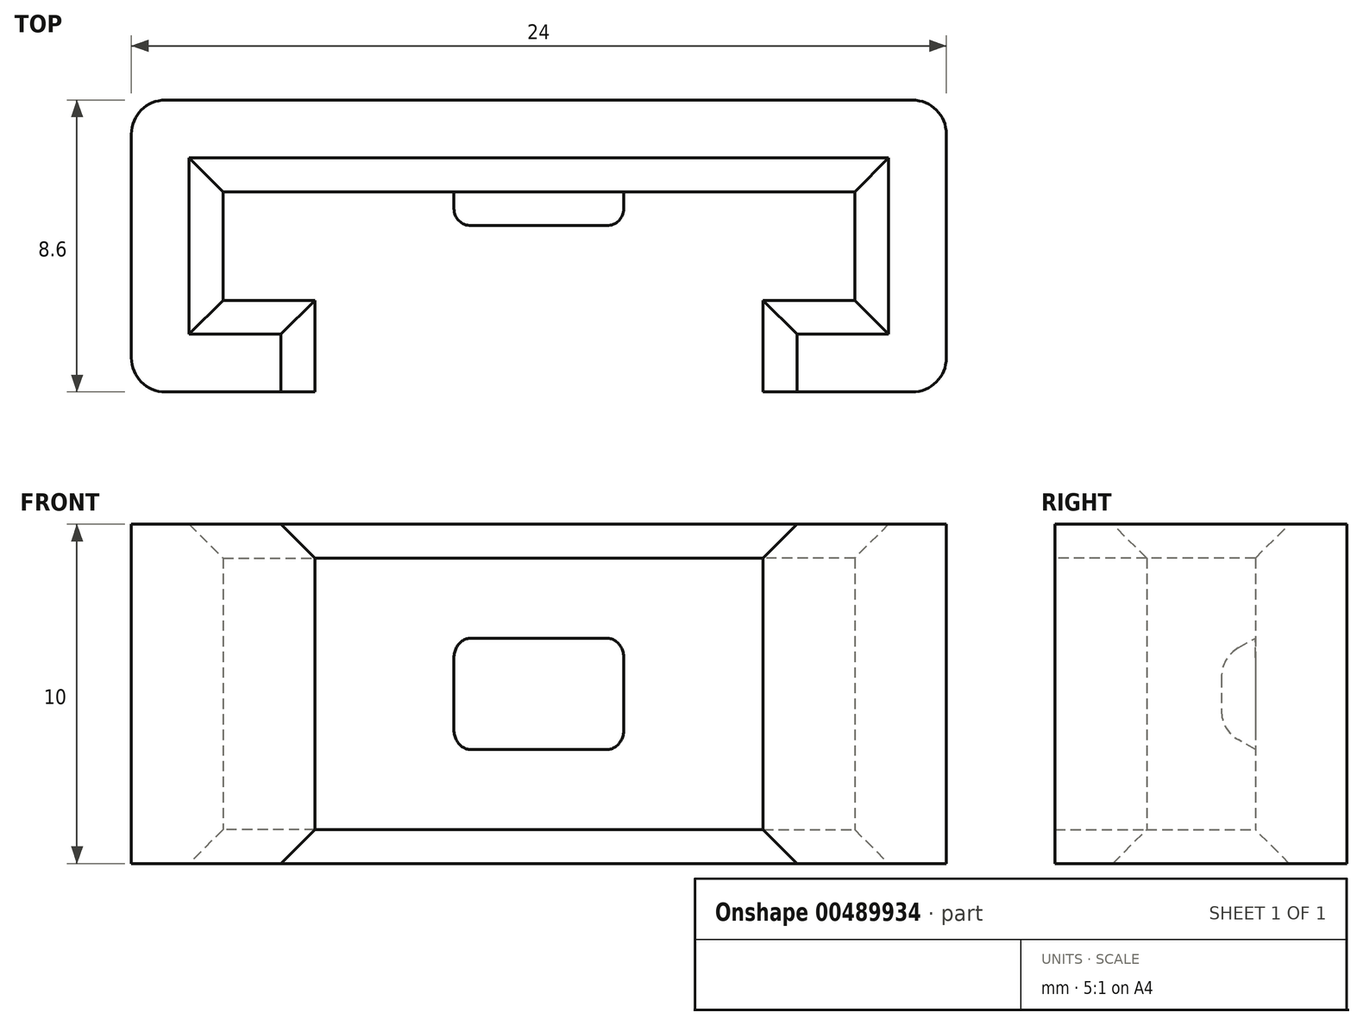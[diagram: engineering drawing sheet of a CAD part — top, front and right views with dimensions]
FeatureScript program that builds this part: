
annotation { "Feature Type Name" : "Feature", "Feature Type Description" : "" }
export const myFeature = defineFeature(function(context is Context, id is Id, definition is map)
    precondition{}
    {
        {
            var Q0;
            Q0=qCreatedBy(makeId("Top.planeOp"),FACE);
            var sketch = newSketch(context, id + "F0", { "sketchPlane" : qUnion([Q0])});
            skLineSegment(sketch, "E0", {"start": v(0, -17.47) * mm, "end": v(0, 25.01) * mm, "construction": true});
            skLineSegment(sketch, "E1", {"start": v(-9.3, -5.9) * mm, "end": v(-6.6, -5.9) * mm});
            skLineSegment(sketch, "E2", {"start": v(-6.6, -5.9) * mm, "end": v(-6.6, -8.6) * mm});
            skLineSegment(sketch, "E3", {"start": v(-6.6, -8.6) * mm, "end": v(-12, -8.6) * mm});
            skLineSegment(sketch, "E4", {"start": v(-12, -8.6) * mm, "end": v(-12, 0) * mm});
            skLineSegment(sketch, "E5", {"start": v(-12, 0) * mm, "end": v(0, 0) * mm});
            skLineSegment(sketch, "E6", {"start": v(-9.3, -5.9) * mm, "end": v(-9.3, -2.7) * mm});
            skLineSegment(sketch, "E7", {"start": v(-9.3, -2.7) * mm, "end": v(0, -2.7) * mm});
            skLineSegment(sketch, "E8.MirrorCS", {"start": v(9.3, -5.9) * mm, "end": v(6.6, -5.9) * mm});
            skLineSegment(sketch, "E9.MirrorCS", {"start": v(9.3, -5.9) * mm, "end": v(9.3, -2.7) * mm});
            skLineSegment(sketch, "E10.MirrorCS", {"start": v(6.6, -5.9) * mm, "end": v(6.6, -8.6) * mm});
            skLineSegment(sketch, "E11.MirrorCS", {"start": v(12, -8.6) * mm, "end": v(12, 0) * mm});
            skLineSegment(sketch, "E12.MirrorCS", {"start": v(6.6, -8.6) * mm, "end": v(12, -8.6) * mm});
            skLineSegment(sketch, "E13.MirrorCS", {"start": v(12, 0) * mm, "end": v(0, 0) * mm});
            skLineSegment(sketch, "E14.MirrorCS", {"start": v(9.3, -2.7) * mm, "end": v(0, -2.7) * mm});
            skSolve(sketch);
        }
        {
            var Q0;
            Q0=qSketchRegion(id+"F0",true);
            extrude(context, id + "F1", {"entities" : qUnion([Q0]), "depth" : 10 * mm});
        }
        {
            var Q0;
            Q0=makeQuery(id+"F1.opExtrude","SWEPT_FACE",FACE,{"disambiguationData":[OSD([sQuery(id+"F0.wireOp",EDGE,"E7"),sQuery(id+"F0.wireOp",EDGE,"E14.MirrorCS")])]});
            var sketch = newSketch(context, id + "F2", { "sketchPlane" : qUnion([Q0])});
            skLineSegment(sketch, "E15", {"start": v(0, 0) * mm, "end": v(0, 10) * mm, "construction": true});
            skLineSegment(sketch, "E16.bottom", {"start": v(2.5, 6.7) * mm, "end": v(-2.5, 6.7) * mm});
            skLineSegment(sketch, "E16.top", {"start": v(2.5, 3.3) * mm, "end": v(-2.5, 3.3) * mm});
            skLineSegment(sketch, "E16.left", {"start": v(2.5, 6.7) * mm, "end": v(2.5, 3.3) * mm});
            skLineSegment(sketch, "E16.right", {"start": v(-2.5, 6.7) * mm, "end": v(-2.5, 3.3) * mm});
            skPoint(sketch, "E16.middle", {"position": v(0, 5) * mm});
            skSolve(sketch);
        }
        {
            var Q0;
            Q0=qSketchRegion(id+"F2",true);
            extrude(context, id + "F3", {"entities" : qUnion([Q0]), "operationType" : NewBodyOperationType.ADD, "depth" : 1 * mm});
        }
        {
            var Q0;
            Q0=makeQuery(id+"F3.opExtrude","CAP_EDGE",EDGE,{"disambiguationData":[OSD([sQuery(id+"F2.wireOp",EDGE,"E16.bottom")])],"isStart":false});
            var Q1;
            Q1=makeQuery(id+"F3.opExtrude","CAP_EDGE",EDGE,{"disambiguationData":[OSD([sQuery(id+"F2.wireOp",EDGE,"E16.top")])],"isStart":false});
            chamfer(context, id + "F4", {"entities" : qUnion([Q0, Q1]), "chamferType" : ChamferType.OFFSET_ANGLE, "width" : 1.1 * mm, "oppositeDirection" : true, "angle" : 30 * degree, "tangentPropagation" : true});
        }
        {
            var Q0;
            {var subQ0=sQuery(id+"F2.wireOp",EDGE,"E16.top");Q0=makeQuery(id+"F4.opChamfer","BLEND_EDGE",EDGE,{"blendedFrom":[makeQuery(id+"F3.opExtrude","CAP_EDGE",EDGE,{"disambiguationData":[OSD([subQ0])],"isStart":false}),makeQuery(id+"F3.opExtrude","CAP_FACE",FACE,{"disambiguationData":[OSD([sQuery(id+"F2.wireOp",EDGE,"E16.bottom"),subQ0,sQuery(id+"F2.wireOp",EDGE,"E16.left"),sQuery(id+"F2.wireOp",EDGE,"E16.right")])],"isStart":false})],"blendedInto":[makeQuery(id+"F3.opExtrude","CAP_FACE",FACE,{"disambiguationData":[OSD([sQuery(id+"F2.wireOp",EDGE,"E16.bottom"),subQ0,sQuery(id+"F2.wireOp",EDGE,"E16.left"),sQuery(id+"F2.wireOp",EDGE,"E16.right")])],"isStart":false})]});}
            var Q1;
            {var subQ0=sQuery(id+"F2.wireOp",EDGE,"E16.bottom");Q1=makeQuery(id+"F4.opChamfer","BLEND_EDGE",EDGE,{"blendedFrom":[makeQuery(id+"F3.opExtrude","CAP_EDGE",EDGE,{"disambiguationData":[OSD([subQ0])],"isStart":false}),makeQuery(id+"F3.opExtrude","CAP_FACE",FACE,{"disambiguationData":[OSD([subQ0,sQuery(id+"F2.wireOp",EDGE,"E16.top"),sQuery(id+"F2.wireOp",EDGE,"E16.left"),sQuery(id+"F2.wireOp",EDGE,"E16.right")])],"isStart":false})],"blendedInto":[makeQuery(id+"F3.opExtrude","CAP_FACE",FACE,{"disambiguationData":[OSD([subQ0,sQuery(id+"F2.wireOp",EDGE,"E16.top"),sQuery(id+"F2.wireOp",EDGE,"E16.left"),sQuery(id+"F2.wireOp",EDGE,"E16.right")])],"isStart":false})]});}
            fillet(context, id + "F5", {"entities" : qUnion([Q0, Q1]), "radius" : 1 * mm, "tangentPropagation" : true, "allowEdgeOverflow" : false});
        }
        {
            var Q0;
            {var subQ0=sQuery(id+"F2.wireOp",EDGE,"E16.left");var subQ1=sQuery(id+"F2.wireOp",EDGE,"E16.top");Q0=makeQuery(id+"F5.opFillet","BLEND_EDGE",EDGE,{"blendedFrom":[makeQuery(id+"F4.opChamfer","BLEND_EDGE",EDGE,{"blendedFrom":[makeQuery(id+"F3.opExtrude","CAP_EDGE",EDGE,{"disambiguationData":[OSD([subQ1])],"isStart":false}),makeQuery(id+"F3.opExtrude","CAP_FACE",FACE,{"disambiguationData":[OSD([sQuery(id+"F2.wireOp",EDGE,"E16.bottom"),subQ1,subQ0,sQuery(id+"F2.wireOp",EDGE,"E16.right")])],"isStart":false})],"blendedInto":[makeQuery(id+"F3.opExtrude","CAP_FACE",FACE,{"disambiguationData":[OSD([sQuery(id+"F2.wireOp",EDGE,"E16.bottom"),subQ1,subQ0,sQuery(id+"F2.wireOp",EDGE,"E16.right")])],"isStart":false})]}),makeQuery(id+"F3.opExtrude","SWEPT_FACE",FACE,{"disambiguationData":[OSD([subQ0])]})],"blendedInto":[makeQuery(id+"F3.opExtrude","SWEPT_FACE",FACE,{"disambiguationData":[OSD([subQ0])]})]});}
            var Q1;
            {var subQ0=sQuery(id+"F2.wireOp",EDGE,"E16.left");var subQ1=sQuery(id+"F2.wireOp",EDGE,"E16.bottom");Q1=makeQuery(id+"F5.opFillet","BLEND_EDGE",EDGE,{"blendedFrom":[makeQuery(id+"F4.opChamfer","BLEND_EDGE",EDGE,{"blendedFrom":[makeQuery(id+"F3.opExtrude","CAP_EDGE",EDGE,{"disambiguationData":[OSD([subQ1])],"isStart":false}),makeQuery(id+"F3.opExtrude","CAP_FACE",FACE,{"disambiguationData":[OSD([subQ1,sQuery(id+"F2.wireOp",EDGE,"E16.top"),subQ0,sQuery(id+"F2.wireOp",EDGE,"E16.right")])],"isStart":false})],"blendedInto":[makeQuery(id+"F3.opExtrude","CAP_FACE",FACE,{"disambiguationData":[OSD([subQ1,sQuery(id+"F2.wireOp",EDGE,"E16.top"),subQ0,sQuery(id+"F2.wireOp",EDGE,"E16.right")])],"isStart":false})]}),makeQuery(id+"F3.opExtrude","SWEPT_FACE",FACE,{"disambiguationData":[OSD([subQ0])]})],"blendedInto":[makeQuery(id+"F3.opExtrude","SWEPT_FACE",FACE,{"disambiguationData":[OSD([subQ0])]})]});}
            var Q2;
            {var subQ0=sQuery(id+"F2.wireOp",EDGE,"E16.right");var subQ1=sQuery(id+"F2.wireOp",EDGE,"E16.top");Q2=makeQuery(id+"F5.opFillet","BLEND_EDGE",EDGE,{"blendedFrom":[makeQuery(id+"F4.opChamfer","BLEND_EDGE",EDGE,{"blendedFrom":[makeQuery(id+"F3.opExtrude","CAP_EDGE",EDGE,{"disambiguationData":[OSD([subQ1])],"isStart":false}),makeQuery(id+"F3.opExtrude","CAP_FACE",FACE,{"disambiguationData":[OSD([sQuery(id+"F2.wireOp",EDGE,"E16.bottom"),subQ1,sQuery(id+"F2.wireOp",EDGE,"E16.left"),subQ0])],"isStart":false})],"blendedInto":[makeQuery(id+"F3.opExtrude","CAP_FACE",FACE,{"disambiguationData":[OSD([sQuery(id+"F2.wireOp",EDGE,"E16.bottom"),subQ1,sQuery(id+"F2.wireOp",EDGE,"E16.left"),subQ0])],"isStart":false})]}),makeQuery(id+"F3.opExtrude","SWEPT_FACE",FACE,{"disambiguationData":[OSD([subQ0])]})],"blendedInto":[makeQuery(id+"F3.opExtrude","SWEPT_FACE",FACE,{"disambiguationData":[OSD([subQ0])]})]});}
            var Q3;
            {var subQ0=sQuery(id+"F2.wireOp",EDGE,"E16.right");var subQ1=sQuery(id+"F2.wireOp",EDGE,"E16.bottom");Q3=makeQuery(id+"F5.opFillet","BLEND_EDGE",EDGE,{"blendedFrom":[makeQuery(id+"F4.opChamfer","BLEND_EDGE",EDGE,{"blendedFrom":[makeQuery(id+"F3.opExtrude","CAP_EDGE",EDGE,{"disambiguationData":[OSD([subQ1])],"isStart":false}),makeQuery(id+"F3.opExtrude","CAP_FACE",FACE,{"disambiguationData":[OSD([subQ1,sQuery(id+"F2.wireOp",EDGE,"E16.top"),sQuery(id+"F2.wireOp",EDGE,"E16.left"),subQ0])],"isStart":false})],"blendedInto":[makeQuery(id+"F3.opExtrude","CAP_FACE",FACE,{"disambiguationData":[OSD([subQ1,sQuery(id+"F2.wireOp",EDGE,"E16.top"),sQuery(id+"F2.wireOp",EDGE,"E16.left"),subQ0])],"isStart":false})]}),makeQuery(id+"F3.opExtrude","SWEPT_FACE",FACE,{"disambiguationData":[OSD([subQ0])]})],"blendedInto":[makeQuery(id+"F3.opExtrude","SWEPT_FACE",FACE,{"disambiguationData":[OSD([subQ0])]})]});}
            fillet(context, id + "F6", {"entities" : qUnion([Q0, Q1, Q2, Q3]), "radius" : 0.5 * mm, "tangentPropagation" : true, "allowEdgeOverflow" : false});
        }
        {
            var Q0;
            Q0=makeQuery(id+"F1.opExtrude","CAP_EDGE",EDGE,{"disambiguationData":[OSD([sQuery(id+"F0.wireOp",EDGE,"E6")])],"isStart":true});
            var Q1;
            Q1=makeQuery(id+"F1.opExtrude","CAP_EDGE",EDGE,{"disambiguationData":[OSD([sQuery(id+"F0.wireOp",EDGE,"E7"),sQuery(id+"F0.wireOp",EDGE,"E14.MirrorCS")])],"isStart":true});
            var Q2;
            Q2=makeQuery(id+"F1.opExtrude","CAP_EDGE",EDGE,{"disambiguationData":[OSD([sQuery(id+"F0.wireOp",EDGE,"E1")])],"isStart":true});
            var Q3;
            Q3=makeQuery(id+"F1.opExtrude","CAP_EDGE",EDGE,{"disambiguationData":[OSD([sQuery(id+"F0.wireOp",EDGE,"E2")])],"isStart":true});
            var Q4;
            Q4=makeQuery(id+"F1.opExtrude","CAP_EDGE",EDGE,{"disambiguationData":[OSD([sQuery(id+"F0.wireOp",EDGE,"E9.MirrorCS")])],"isStart":true});
            var Q5;
            Q5=makeQuery(id+"F1.opExtrude","CAP_EDGE",EDGE,{"disambiguationData":[OSD([sQuery(id+"F0.wireOp",EDGE,"E8.MirrorCS")])],"isStart":true});
            var Q6;
            Q6=makeQuery(id+"F1.opExtrude","CAP_EDGE",EDGE,{"disambiguationData":[OSD([sQuery(id+"F0.wireOp",EDGE,"E10.MirrorCS")])],"isStart":true});
            var Q7;
            Q7=makeQuery(id+"F1.opExtrude","CAP_EDGE",EDGE,{"disambiguationData":[OSD([sQuery(id+"F0.wireOp",EDGE,"E6")])],"isStart":false});
            var Q8;
            Q8=makeQuery(id+"F1.opExtrude","CAP_EDGE",EDGE,{"disambiguationData":[OSD([sQuery(id+"F0.wireOp",EDGE,"E1")])],"isStart":false});
            var Q9;
            Q9=makeQuery(id+"F1.opExtrude","CAP_EDGE",EDGE,{"disambiguationData":[OSD([sQuery(id+"F0.wireOp",EDGE,"E2")])],"isStart":false});
            var Q10;
            Q10=makeQuery(id+"F1.opExtrude","CAP_EDGE",EDGE,{"disambiguationData":[OSD([sQuery(id+"F0.wireOp",EDGE,"E7"),sQuery(id+"F0.wireOp",EDGE,"E14.MirrorCS")])],"isStart":false});
            var Q11;
            Q11=makeQuery(id+"F1.opExtrude","CAP_EDGE",EDGE,{"disambiguationData":[OSD([sQuery(id+"F0.wireOp",EDGE,"E9.MirrorCS")])],"isStart":false});
            var Q12;
            Q12=makeQuery(id+"F1.opExtrude","CAP_EDGE",EDGE,{"disambiguationData":[OSD([sQuery(id+"F0.wireOp",EDGE,"E8.MirrorCS")])],"isStart":false});
            var Q13;
            Q13=makeQuery(id+"F1.opExtrude","CAP_EDGE",EDGE,{"disambiguationData":[OSD([sQuery(id+"F0.wireOp",EDGE,"E10.MirrorCS")])],"isStart":false});
            chamfer(context, id + "F7", {"entities" : qUnion([Q0, Q1, Q2, Q3, Q4, Q5, Q6, Q7, Q8, Q9, Q10, Q11, Q12, Q13]), "width" : 1 * mm, "tangentPropagation" : true});
        }
        {
            var Q0;
            Q0=makeQuery(id+"F1.opExtrude","SWEPT_EDGE",EDGE,{"disambiguationData":[OSD([sQuery(id+"F0.wireOp",EDGE,"E3"),sQuery(id+"F0.wireOp",EDGE,"E4")])]});
            var Q1;
            Q1=makeQuery(id+"F1.opExtrude","SWEPT_EDGE",EDGE,{"disambiguationData":[OSD([sQuery(id+"F0.wireOp",EDGE,"E11.MirrorCS"),sQuery(id+"F0.wireOp",EDGE,"E12.MirrorCS")])]});
            var Q2;
            Q2=makeQuery(id+"F1.opExtrude","SWEPT_EDGE",EDGE,{"disambiguationData":[OSD([sQuery(id+"F0.wireOp",EDGE,"E4"),sQuery(id+"F0.wireOp",EDGE,"E5")])]});
            var Q3;
            Q3=makeQuery(id+"F1.opExtrude","SWEPT_EDGE",EDGE,{"disambiguationData":[OSD([sQuery(id+"F0.wireOp",EDGE,"E11.MirrorCS"),sQuery(id+"F0.wireOp",EDGE,"E13.MirrorCS")])]});
            fillet(context, id + "F8", {"entities" : qUnion([Q0, Q1, Q2, Q3]), "radius" : 1 * mm, "tangentPropagation" : true, "allowEdgeOverflow" : false});
        }
    });
